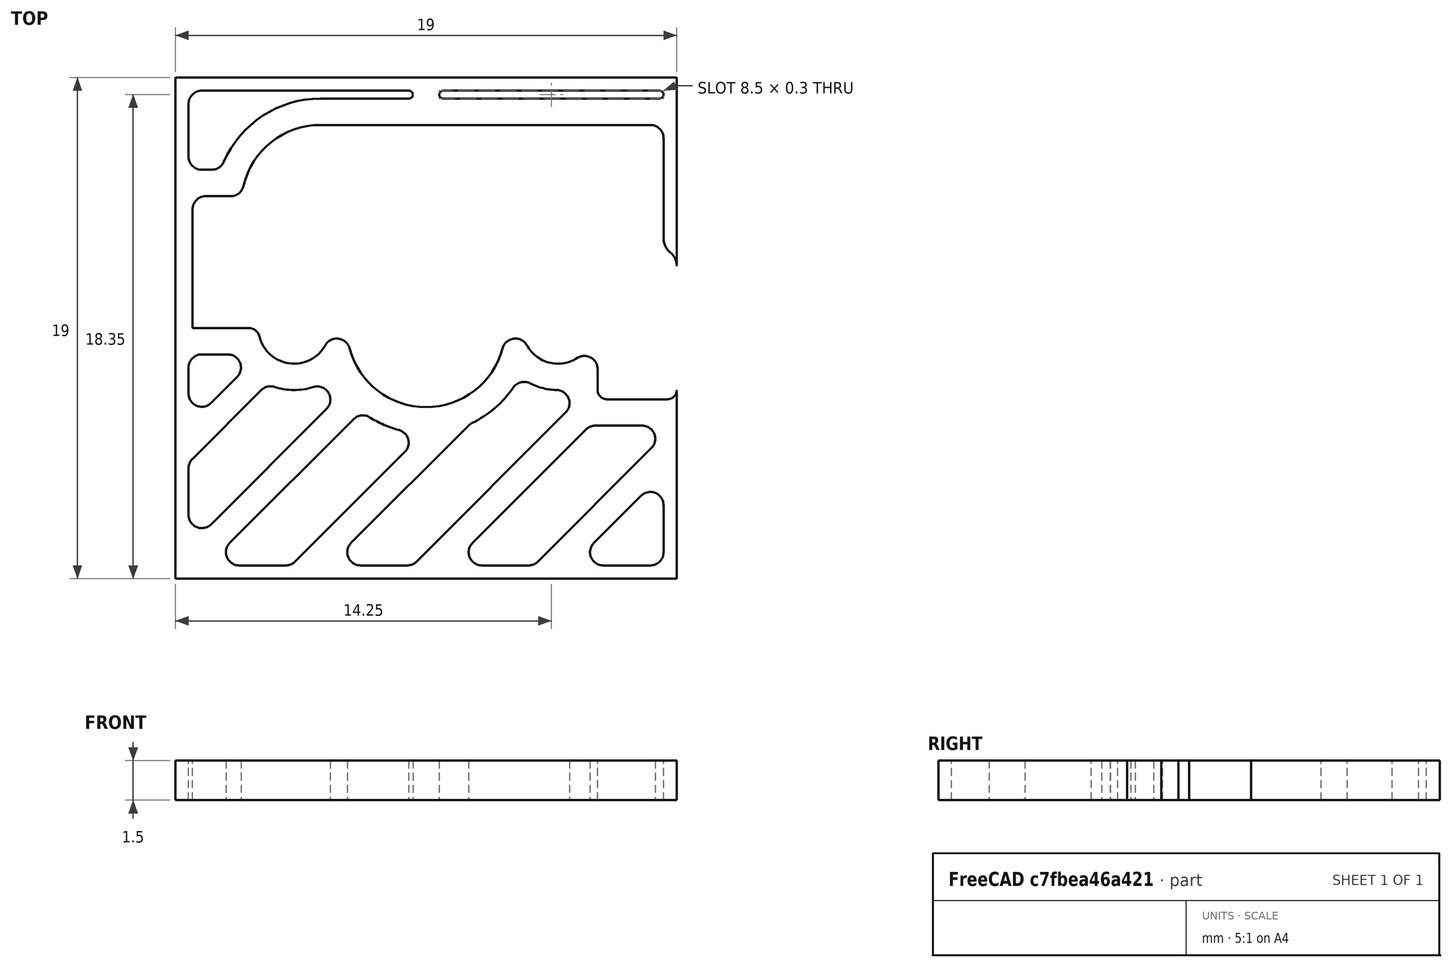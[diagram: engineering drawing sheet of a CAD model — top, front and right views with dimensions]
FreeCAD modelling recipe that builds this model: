
FCSTD DOCUMENT  (FreeCAD 0.22R36807 (Git))
Label: key-v2
License: All rights reserved
LicenseURL: https://en.wikipedia.org/wiki/All_rights_reserved
objects: Part::Part2DObjectPython×3, Sketcher::SketchObject×1, PartDesign::Pad×1, PartDesign::Body×1, Spreadsheet::Sheet×1
note: 7 computed .brp shape members not serialized (recipe doc carries the construction recipe); baked Part::Feature solids carry a one-line shape summary decoded from their .brp

FEATURE [Sketcher::SketchObject] Sketch  label="base"
  FullyConstrained = false
  sketch-geometry (148):
    g0: LineSegment StartX=-9.5 StartY=-9.5 StartZ=0 EndX=9.5 EndY=-9.5 EndZ=0
    g1: LineSegment StartX=9.5 StartY=-9.5 StartZ=0 EndX=9.5 EndY=9.5 EndZ=0
    g2: LineSegment StartX=9.5 StartY=9.5 StartZ=0 EndX=-9.5 EndY=9.5 EndZ=0
    g3: LineSegment StartX=-9.5 StartY=9.5 StartZ=0 EndX=-9.5 EndY=-9.5 EndZ=0
    g4: GeomPoint X=-1.9e-14 Y=1.95e-14 Z=0
    g5: Circle CenterX=-3.81 CenterY=2.54 CenterZ=0 NormalX=0 NormalY=0 NormalZ=1 AngleXU=0 Radius=1.5
    g6: Circle CenterX=2.54 CenterY=5.08 CenterZ=0 NormalX=0 NormalY=0 NormalZ=1 AngleXU=0 Radius=1.5
    g7: Circle CenterX=-1.9e-14 CenterY=1.95e-14 CenterZ=0 NormalX=0 NormalY=0 NormalZ=1 AngleXU=0 Radius=2
    g8: Circle CenterX=5 CenterY=-2.49e-14 CenterZ=0 NormalX=0 NormalY=0 NormalZ=1 AngleXU=0 Radius=1
    g9: Circle CenterX=-5 CenterY=-2.4746e-12 CenterZ=0 NormalX=0 NormalY=0 NormalZ=1 AngleXU=0 Radius=1
    g10: GeomPoint X=-8.5 Y=1 Z=0
    g11: GeomPoint X=-8.5 Y=4 Z=0
    g12: GeomPoint X=-6 Y=4 Z=0
    g13: GeomPoint X=-2.5 Y=1 Z=0
    g14: GeomPoint X=-0.4 Y=2.9 Z=0
    g15: GeomPoint X=4.5 Y=2.9 Z=0
    g16: GeomPoint X=4.5 Y=3.6 Z=0
    g17: GeomPoint X=7.1 Y=6.7 Z=0
    g18: GeomPoint X=-4 Y=6.7 Z=0
    g19: LineSegment StartX=-8.5 StartY=1 StartZ=0 EndX=-2.5 EndY=1 EndZ=0
    g20: LineSegment StartX=-8.5 StartY=1 StartZ=0 EndX=-8.5 EndY=4 EndZ=0
    g21: LineSegment StartX=-8.5 StartY=4 StartZ=0 EndX=-6 EndY=4 EndZ=0
    g22: LineSegment StartX=-6 StartY=4 StartZ=0 EndX=-6 EndY=4.7 EndZ=0
    g23: LineSegment StartX=-4 StartY=6.7 StartZ=0 EndX=7.1 EndY=6.7 EndZ=0
    g24: LineSegment StartX=7.1 StartY=6.7 StartZ=0 EndX=7.1 EndY=3.6 EndZ=0
    g25: LineSegment StartX=7.1 StartY=3.6 StartZ=0 EndX=4.5 EndY=3.6 EndZ=0
    g26: LineSegment StartX=4.5 StartY=2.9 StartZ=0 EndX=4.5 EndY=3.6 EndZ=0
    g27: LineSegment StartX=4.5 StartY=2.9 StartZ=0 EndX=-0.4 EndY=2.9 EndZ=0
    g28: ArcOfCircle CenterX=-0.400861 CenterY=0.790425 CenterZ=0 NormalX=0 NormalY=0 NormalZ=1 AngleXU=0 Radius=2.10958 StartAngle=1.57039 EndAngle=3.04208
    g29: LineSegment StartX=-8.14645 StartY=-7.43934 StartZ=0 EndX=-3.77376 EndY=-3.06666 EndZ=0
    g30: LineSegment StartX=-7.43934 StartY=-8.14645 StartZ=0 EndX=-2.74887 EndY=-3.45597 EndZ=0
    g31: ArcOfCircle CenterX=-1.9e-14 CenterY=1.95e-14 CenterZ=0 NormalX=0 NormalY=0 NormalZ=1 AngleXU=0 Radius=3 StartAngle=3.40116 EndAngle=6.02361
    g32: ArcOfCircle CenterX=-1.9e-14 CenterY=1.95e-14 CenterZ=0 NormalX=0 NormalY=0 NormalZ=1 AngleXU=0 Radius=4 StartAngle=4.15108 EndAngle=4.45128
    g33: LineSegment StartX=-1.9e-14 StartY=1.95e-14 StartZ=0 EndX=-9.5 EndY=-9.5 EndZ=0
    g34: LineSegment StartX=-7.51422 StartY=-1 StartZ=0 EndX=-8.5 EndY=-1 EndZ=0
    g35: ArcOfCircle CenterX=-2.39531 CenterY=-3.80953 CenterZ=0 NormalX=0 NormalY=0 NormalZ=1 AngleXU=0 Radius=0.5 StartAngle=1.00949 EndAngle=2.35619
    g36: ArcOfCircle CenterX=-1.16168 CenterY=-4.34747 CenterZ=0 NormalX=0 NormalY=0 NormalZ=1 AngleXU=0 Radius=0.5 StartAngle=5.49779 EndAngle=7.59287
    g37: ArcOfCircle CenterX=-7.08579 CenterY=-8.5 CenterZ=0 NormalX=0 NormalY=0 NormalZ=1 AngleXU=0 Radius=0.5 StartAngle=2.35619 EndAngle=4.71239
    g38: GeomPoint X=-8.29289 Y=-9 Z=0
    g39: LineSegment StartX=-9 StartY=-1.5 StartZ=0 EndX=-9 EndY=-2.48578 EndZ=0
    g40: ArcOfCircle CenterX=-8.5 CenterY=-1.5 CenterZ=0 NormalX=0 NormalY=0 NormalZ=1 AngleXU=0 Radius=0.5 StartAngle=1.5708 EndAngle=3.14159
    g41: GeomPoint X=-9 Y=-1 Z=0
    g42: ArcOfCircle CenterX=-8.5 CenterY=-7.08579 CenterZ=0 NormalX=0 NormalY=0 NormalZ=1 AngleXU=0 Radius=0.5 StartAngle=3.14159 EndAngle=5.49779
    g43: GeomPoint X=-9 Y=-8.29289 Z=0
    g44: ArcOfCircle CenterX=-5 CenterY=-2.4746e-12 CenterZ=0 NormalX=0 NormalY=0 NormalZ=1 AngleXU=0 Radius=1.35 StartAngle=3.38311 EndAngle=5.77615
    g45: ArcOfCircle CenterX=-3.38275 CenterY=-0.898333 CenterZ=0 NormalX=0 NormalY=0 NormalZ=1 AngleXU=0 Radius=0.5 StartAngle=0.259572 EndAngle=2.63456
    g46: ArcOfCircle CenterX=-1.9e-14 CenterY=1.95e-14 CenterZ=0 NormalX=0 NormalY=0 NormalZ=1 AngleXU=0 Radius=4 StartAngle=5.16472 EndAngle=5.68269
    g47: ArcOfCircle CenterX=1.96677 CenterY=-4.04745 CenterZ=0 NormalX=0 NormalY=0 NormalZ=1 AngleXU=0 Radius=0.5 StartAngle=2.02312 EndAngle=2.35619
    g48: ArcOfCircle CenterX=8.5 CenterY=-8.5 CenterZ=0 NormalX=0 NormalY=0 NormalZ=1 AngleXU=0 Radius=0.5 StartAngle=4.71239 EndAngle=6.28319
    g49: ArcOfCircle CenterX=3.71275 CenterY=-2.54273 CenterZ=0 NormalX=0 NormalY=0 NormalZ=1 AngleXU=0 Radius=0.5 StartAngle=1.10216 EndAngle=2.5411
    g50: LineSegment StartX=6.85 StartY=2.35 StartZ=0 EndX=6.85 EndY=-2.35 EndZ=0
    g51: LineSegment StartX=6.85 StartY=-2.35 StartZ=0 EndX=9.15 EndY=-2.35 EndZ=0
    g52: LineSegment StartX=9.15 StartY=-2.35 StartZ=0 EndX=9.15 EndY=2.35 EndZ=0
    g53: LineSegment StartX=9.15 StartY=2.35 StartZ=0 EndX=6.85 EndY=2.35 EndZ=0
    g54: LineSegment StartX=8.18579 StartY=-3.7 StartZ=0 EndX=6.41421 EndY=-3.7 EndZ=0
    g55: ArcOfCircle CenterX=5 CenterY=-2.49e-14 CenterZ=0 NormalX=0 NormalY=0 NormalZ=1 AngleXU=0 Radius=1.35 StartAngle=3.64863 EndAngle=5.28347
    g56: ArcOfCircle CenterX=3.38275 CenterY=-0.898333 CenterZ=0 NormalX=0 NormalY=0 NormalZ=1 AngleXU=0 Radius=0.5 StartAngle=0.507033 EndAngle=2.88202
    g57: ArcOfCircle CenterX=4.93649 CenterY=-2.84929 CenterZ=0 NormalX=0 NormalY=0 NormalZ=1 AngleXU=0 Radius=0.5 StartAngle=5.49779 EndAngle=7.8317
    g58: ArcOfCircle CenterX=6.85 CenterY=-2.35 CenterZ=0 NormalX=0 NormalY=0 NormalZ=1 AngleXU=0 Radius=0.35 StartAngle=3.14159 EndAngle=4.71239
    g59: LineSegment StartX=6.5 StartY=-2.35 StartZ=0 EndX=6.5 EndY=-1.55644 EndZ=0
    g60: ArcOfCircle CenterX=6 CenterY=-1.55644 CenterZ=0 NormalX=0 NormalY=0 NormalZ=1 AngleXU=0 Radius=0.5 StartAngle=2e-16 EndAngle=2.14188
    g61: LineSegment StartX=9.5 StartY=-2.35 StartZ=0 EndX=9.5 EndY=-9.5 EndZ=0
    g62: LineSegment StartX=9 StartY=3.39614 StartZ=0 EndX=9 EndY=7.2 EndZ=0
    g63: LineSegment StartX=8.5 StartY=7.7 StartZ=0 EndX=-4 EndY=7.7 EndZ=0
    g64: LineSegment StartX=-8.85 StartY=1.9e-15 StartZ=0 EndX=-8.85 EndY=4.5 EndZ=0
    g65: LineSegment StartX=-8.35 StartY=5 StartZ=0 EndX=-7.40735 EndY=5 EndZ=0
    g66: ArcOfCircle CenterX=9.15 CenterY=-2.35 CenterZ=0 NormalX=0 NormalY=0 NormalZ=1 AngleXU=0 Radius=0.35 StartAngle=4.71239 EndAngle=6.28319
    g67: LineSegment StartX=6.85 StartY=-2.7 StartZ=0 EndX=9.15 EndY=-2.7 EndZ=0
    g68: GeomPoint X=-8.85 Y=-0.7 Z=0
    g69: ArcOfCircle CenterX=-8.35 CenterY=4.5 CenterZ=0 NormalX=0 NormalY=0 NormalZ=1 AngleXU=0 Radius=0.5 StartAngle=1.5708 EndAngle=3.14159
    g70: GeomPoint X=-8.85 Y=5 Z=0
    g71: ArcOfCircle CenterX=-7.40735 CenterY=5.5 CenterZ=0 NormalX=0 NormalY=0 NormalZ=1 AngleXU=0 Radius=0.5 StartAngle=4.71239 EndAngle=6.05258
    g72: ArcOfCircle CenterX=8.5 CenterY=7.2 CenterZ=0 NormalX=0 NormalY=0 NormalZ=1 AngleXU=0 Radius=0.5 StartAngle=-9e-16 EndAngle=1.5708
    g73: GeomPoint X=9 Y=7.7 Z=0
    g74: LineSegment StartX=-9 StartY=8.5 StartZ=0 EndX=-9 EndY=6.5 EndZ=0
    g75: LineSegment StartX=-8.5 StartY=6 StartZ=0 EndX=-8.12432 EndY=6 EndZ=0
    g76: LineSegment StartX=-8.5 StartY=9 StartZ=0 EndX=-0.65 EndY=9 EndZ=0
    g77: ArcOfCircle CenterX=-8.12432 CenterY=6.5 CenterZ=0 NormalX=0 NormalY=0 NormalZ=1 AngleXU=0 Radius=0.5 StartAngle=4.71239 EndAngle=5.87167
    g78: ArcOfCircle CenterX=-8.5 CenterY=6.5 CenterZ=0 NormalX=0 NormalY=0 NormalZ=1 AngleXU=0 Radius=0.5 StartAngle=3.14159 EndAngle=4.71239
    g79: GeomPoint X=-9 Y=6 Z=0
    g80: ArcOfCircle CenterX=-8.5 CenterY=8.5 CenterZ=0 NormalX=0 NormalY=0 NormalZ=1 AngleXU=0 Radius=0.5 StartAngle=1.5708 EndAngle=3.14159
    g81: GeomPoint X=-9 Y=9 Z=0
    g82: ArcOfCircle CenterX=-4.12732 CenterY=-2.7131 CenterZ=0 NormalX=0 NormalY=0 NormalZ=1 AngleXU=0 Radius=0.5 StartAngle=5.49779 EndAngle=8.16519
    g83: ArcOfCircle CenterX=5 CenterY=-2.49e-14 CenterZ=0 NormalX=0 NormalY=0 NormalZ=1 AngleXU=0 Radius=2.35 StartAngle=4.24376 EndAngle=4.6901
    g84: LineSegment StartX=-4 StartY=8.7 StartZ=0 EndX=-0.65 EndY=8.7 EndZ=0
    g85: ArcOfCircle CenterX=8.85 CenterY=8.85 CenterZ=0 NormalX=0 NormalY=0 NormalZ=1 AngleXU=0 Radius=0.15 StartAngle=4.71239 EndAngle=7.85398
    g86: LineSegment StartX=6.85 StartY=-2.35 StartZ=0 EndX=-0.3 EndY=-9.5 EndZ=0
    g87: LineSegment StartX=6.06066 StartY=-3.84645 StartZ=0 EndX=1.76066 EndY=-8.14645 EndZ=0
    g88: LineSegment StartX=5.29005 StartY=-3.20285 StartZ=0 EndX=-0.36066 EndY=-8.85355 EndZ=0
    g89: LineSegment StartX=-2.83934 StartY=-8.14645 StartZ=0 EndX=1.61321 EndY=-3.69389 EndZ=0
    g90: LineSegment StartX=-4.96066 StartY=-8.85355 StartZ=0 EndX=-0.80813 EndY=-4.70102 EndZ=0
    g91: LineSegment StartX=-0.714214 StartY=-9 StartZ=0 EndX=-2.48579 EndY=-9 EndZ=0
    g92: LineSegment StartX=-5.31421 StartY=-9 StartZ=0 EndX=-7.08579 EndY=-9 EndZ=0
    g93: LineSegment StartX=-4.9 StartY=-9.5 StartZ=0 EndX=4.6 EndY=1.95e-14 EndZ=0
    g94: LineSegment StartX=-2.45 StartY=-2.45 StartZ=0 EndX=2.15 EndY=-7.05 EndZ=0
    g95: LineSegment StartX=4.3 StartY=-9.5 StartZ=0 EndX=9.5 EndY=-4.3 EndZ=0
    g96: LineSegment StartX=0.975 StartY=-3.625 StartZ=0 EndX=5.575 EndY=-8.225 EndZ=0
    g97: LineSegment StartX=4.23934 StartY=-8.85355 StartZ=0 EndX=8.53934 EndY=-4.55355 EndZ=0
    g98: LineSegment StartX=6.36066 StartY=-8.14645 StartZ=0 EndX=8.14645 EndY=-6.36066 EndZ=0
    g99: LineSegment StartX=9 StartY=-6.71421 StartZ=0 EndX=9 EndY=-8.5 EndZ=0
    g100: LineSegment StartX=6.71421 StartY=-9 StartZ=0 EndX=8.5 EndY=-9 EndZ=0
    g101: LineSegment StartX=3.88579 StartY=-9 StartZ=0 EndX=2.11421 EndY=-9 EndZ=0
    g102: ArcOfCircle CenterX=8.18579 CenterY=-4.2 CenterZ=0 NormalX=0 NormalY=0 NormalZ=1 AngleXU=0 Radius=0.5 StartAngle=5.49779 EndAngle=7.85398
    g103: ArcOfCircle CenterX=6.41421 CenterY=-4.2 CenterZ=0 NormalX=0 NormalY=0 NormalZ=1 AngleXU=0 Radius=0.5 StartAngle=1.5708 EndAngle=2.35619
    g104: GeomPoint X=6.20711 Y=-3.7 Z=0
    g105: ArcOfCircle CenterX=8.5 CenterY=-6.71421 CenterZ=0 NormalX=0 NormalY=0 NormalZ=1 AngleXU=0 Radius=0.5 StartAngle=-9e-16 EndAngle=2.35619
    g106: GeomPoint X=9 Y=-5.50711 Z=0
    g107: ArcOfCircle CenterX=6.71421 CenterY=-8.5 CenterZ=0 NormalX=0 NormalY=0 NormalZ=1 AngleXU=0 Radius=0.5 StartAngle=2.35619 EndAngle=4.71239
    g108: GeomPoint X=5.50711 Y=-9 Z=0
    g109: ArcOfCircle CenterX=3.88579 CenterY=-8.5 CenterZ=0 NormalX=0 NormalY=0 NormalZ=1 AngleXU=0 Radius=0.5 StartAngle=4.71239 EndAngle=5.49779
    g110: GeomPoint X=4.09289 Y=-9 Z=0
    g111: ArcOfCircle CenterX=2.11421 CenterY=-8.5 CenterZ=0 NormalX=0 NormalY=0 NormalZ=1 AngleXU=0 Radius=0.5 StartAngle=2.35619 EndAngle=4.71239
    g112: GeomPoint X=0.907107 Y=-9 Z=0
    g113: ArcOfCircle CenterX=-2.48579 CenterY=-8.5 CenterZ=0 NormalX=0 NormalY=0 NormalZ=1 AngleXU=0 Radius=0.5 StartAngle=2.35619 EndAngle=4.71239
    g114: GeomPoint X=-3.69289 Y=-9 Z=0
    g115: ArcOfCircle CenterX=-0.714214 CenterY=-8.5 CenterZ=0 NormalX=0 NormalY=0 NormalZ=1 AngleXU=0 Radius=0.5 StartAngle=4.71239 EndAngle=5.49779
    g116: GeomPoint X=-0.507107 Y=-9 Z=0
    g117: ArcOfCircle CenterX=-5.31421 CenterY=-8.5 CenterZ=0 NormalX=0 NormalY=0 NormalZ=1 AngleXU=0 Radius=0.5 StartAngle=4.71239 EndAngle=5.49779
    g118: GeomPoint X=-5.10711 Y=-9 Z=0
    g119: LineSegment StartX=-9.5 StartY=-9.5 StartZ=0 EndX=9.5 EndY=-9.5 EndZ=0
    g120: ArcOfCircle CenterX=9.67221 CenterY=3.39614 CenterZ=0 NormalX=0 NormalY=0 NormalZ=1 AngleXU=0 Radius=0.672207 StartAngle=3.14159 EndAngle=4.03329
    g121: ArcOfCircle CenterX=8.82779 CenterY=2.35 CenterZ=0 NormalX=0 NormalY=0 NormalZ=1 AngleXU=0 Radius=0.672207 StartAngle=0 EndAngle=0.891699
    g122: LineSegment StartX=9.5 StartY=2.35 StartZ=0 EndX=9.09006 EndY=3.06004 EndZ=0
    g123: LineSegment StartX=9.5 StartY=2.35 StartZ=0 EndX=9.5 EndY=9.5 EndZ=0
    g124: LineSegment StartX=9.5 StartY=9.5 StartZ=0 EndX=-9.5 EndY=9.5 EndZ=0
    g125: ArcOfCircle CenterX=-4 CenterY=4.7 CenterZ=0 NormalX=0 NormalY=0 NormalZ=1 AngleXU=0 Radius=4 StartAngle=1.5708 EndAngle=2.73008
    g126: ArcOfCircle CenterX=-4 CenterY=4.7 CenterZ=0 NormalX=0 NormalY=0 NormalZ=1 AngleXU=0 Radius=3 StartAngle=1.5708 EndAngle=2.91098
    g127: ArcOfCircle CenterX=-4 CenterY=4.7 CenterZ=0 NormalX=0 NormalY=0 NormalZ=1 AngleXU=0 Radius=2 StartAngle=1.5708 EndAngle=3.14159
    g128: ArcOfCircle CenterX=-0.65 CenterY=8.85 CenterZ=0 NormalX=0 NormalY=0 NormalZ=1 AngleXU=0 Radius=0.15 StartAngle=4.71239 EndAngle=7.85398
    g129: LineSegment StartX=0.65 StartY=9 StartZ=0 EndX=8.85 EndY=9 EndZ=0
    g130: LineSegment StartX=0.65 StartY=8.7 StartZ=0 EndX=8.85 EndY=8.7 EndZ=0
    g131: ArcOfCircle CenterX=0.65 CenterY=8.85 CenterZ=0 NormalX=0 NormalY=0 NormalZ=1 AngleXU=0 Radius=0.15 StartAngle=1.5708 EndAngle=4.71239
    g132: LineSegment StartX=-9.5 StartY=-4.89999 StartZ=0 EndX=-4.60001 EndY=1.95e-14 EndZ=0
    g133: LineSegment StartX=-7.05 StartY=-2.45 StartZ=0 EndX=-2.45 EndY=-7.05 EndZ=0
    g134: LineSegment StartX=-8.85355 StartY=-4.96065 StartZ=0 EndX=-6.24601 EndY=-2.35311 EndZ=0
    g135: ArcOfCircle CenterX=-5 CenterY=-2.4746e-12 CenterZ=0 NormalX=0 NormalY=0 NormalZ=1 AngleXU=0 Radius=2.35 StartAngle=4.39389 EndAngle=5.02359
    g136: LineSegment StartX=-9 StartY=-5.31421 StartZ=0 EndX=-9 EndY=-7.08579 EndZ=0
    g137: LineSegment StartX=-8.14645 StartY=-2.83933 StartZ=0 EndX=-7.16067 EndY=-1.85355 EndZ=0
    g138: ArcOfCircle CenterX=-5.89246 CenterY=-2.70666 CenterZ=0 NormalX=0 NormalY=0 NormalZ=1 AngleXU=0 Radius=0.5 StartAngle=1.2523 EndAngle=2.35619
    g139: ArcOfCircle CenterX=-8.5 CenterY=-5.31421 CenterZ=0 NormalX=0 NormalY=0 NormalZ=1 AngleXU=0 Radius=0.5 StartAngle=2.35619 EndAngle=3.14159
    g140: GeomPoint X=-9 Y=-5.1071 Z=0
    g141: ArcOfCircle CenterX=-8.5 CenterY=-2.48578 CenterZ=0 NormalX=0 NormalY=0 NormalZ=1 AngleXU=0 Radius=0.5 StartAngle=3.14159 EndAngle=5.49779
    g142: GeomPoint X=-9 Y=-3.69289 Z=0
    g143: ArcOfCircle CenterX=-7.51422 CenterY=-1.5 CenterZ=0 NormalX=0 NormalY=0 NormalZ=1 AngleXU=0 Radius=0.5 StartAngle=5.49779 EndAngle=7.85398
    g144: GeomPoint X=-6.30711 Y=-1 Z=0
    g145: LineSegment StartX=-9.5 StartY=9.5 StartZ=0 EndX=-9.5 EndY=-9.5 EndZ=0
    g146: LineSegment StartX=-8.85 StartY=1.9e-15 StartZ=0 EndX=-6.72288 EndY=1.9e-15 EndZ=0
    g147: ArcOfCircle CenterX=-6.72288 CenterY=-0.424382 CenterZ=0 NormalX=0 NormalY=0 NormalZ=1 AngleXU=0 Radius=0.424382 StartAngle=0.241513 EndAngle=1.5708
  constraints (336):
    c: Coincident(g0,g1)
    c: Coincident(g1,g2)
    c: Coincident(g2,g3)
    c: Horizontal(g0)
    c: Horizontal(g2)
    c: Vertical(g1)
    c: Symmetric(g2,g0,g4)
    c: Coincident(g4,g-1)
    c: Coincident(g7,g4)
    c: PointOnObject(g8,g-1)
    c: Equal(g5,g6)
    c: Symmetric(g8,g9,g-2)
    c: Equal(g9,g8)
    c: DistanceX(g-1,g6) = 2.54
    c: Distance(g6,g-1) = 5.08
    c: DistanceX(g2,g2) = 19
    c: Equal(g2,g3)
    c: Distance(g5,g-2) = 3.81
    c: Distance(g5,g-1) = 2.54
    c: Distance(g9,g-2) = 5
    c: Distance(g10,g-1) = 1
    c: Coincident(g19,g10)
    c: Coincident(g19,g13)
    c: Horizontal(g19)
    c: Distance(g10,g-2) = 8.5
    c: Coincident(g20,g10)
    c: Coincident(g20,g11)
    c: Vertical(g20)
    c: Distance(g11,g-1) = 4
    c: Coincident(g21,g11)
    c: Coincident(g21,g12)
    c: Horizontal(g21)
    c: Distance(g12,g-2) = 6
    c: Distance(g18,g-2) = 4
    c: DistanceY(g-1,g18) = 6.7
    c: Coincident(g22,g12)
    c: Vertical(g22)
    c: Coincident(g23,g18)
    c: Coincident(g23,g17)
    c: Horizontal(g23)
    c: DistanceX(g-1,g17) = 7.1
    c: Coincident(g24,g17)
    c: Vertical(g24)
    c: Distance(g24,g-1) = 3.6
    c: Coincident(g25,g24)
    c: Coincident(g25,g16)
    c: Coincident(g26,g15)
    c: Coincident(g26,g16)
    c: Coincident(g27,g15)
    c: Coincident(g27,g14)
    c: Horizontal(g25)
    c: Horizontal(g27)
    c: Vertical(g26)
    c: Distance(g-2,g26) = 4.5
    c: Distance(g15,g-1) = 2.9
    c: Distance(g14,g-2) = 0.4
    c: Distance(g13,g-2) = 2.5
    c: Coincident(g28,g14)
    c: Coincident(g28,g13)
    c: Diameter(g6) = 3
    c: Diameter(g9) = 2
    c: Diameter(g7) = 4
    c: Parallel(g30,g29)
    c: Distance(g31,g7) = 1
    c: Coincident(g32,g31)
    c: Symmetric(g38,g43,g33)
    c: Horizontal(g34)
    c: Distance(g43,g30) = 1
    c: Tangent(g30,g35) = 1.5708
    c: Tangent(g32,g35) = 1.5708
    c: Tangent(g32,g36) = 1.5708
    c: PointOnObject(g38,g30)
    c: Tangent(g30,g37) = 1.5708
    c: Vertical(g39)
    c: PointOnObject(g41,g34)
    c: PointOnObject(g41,g39)
    c: Tangent(g34,g40) = -1.5708
    c: Tangent(g39,g40) = -1.5708
    c: PointOnObject(g43,g39)
    c: PointOnObject(g43,g29)
    c: Tangent(g29,g42) = -1.5708
    c: Equal(g42,g35)
    c: Equal(g35,g36)
    c: Coincident(g44,g9)
    c: Radius(g40) = 0.5
    c: Distance(g32,g31) = 1
    c: Tangent(g45,g31) = 1.5708
    c: Tangent(g45,g44) = 1.5708
    c: Coincident(g46,g31)
    c: Equal(g46,g32)
    c: Equal(g49,g36)
    c: Coincident(g50,g51)
    c: Coincident(g51,g52)
    c: Coincident(g52,g53)
    c: Coincident(g53,g50)
    c: Vertical(g52)
    c: Horizontal(g51)
    c: Horizontal(g53)
    c: Distance(g50,g-2) = 6.85
    c: Distance(g50,g-1) = 2.35
    c: Symmetric(g50,g50,g-1)
    c: DistanceX(g53,g53) = 2.3
    c: Horizontal(g54)
    c: Coincident(g55,g8)
    c: Distance(g55,g8) = 0.35
    c: Tangent(g56,g31) = 1.5708
    c: Tangent(g56,g55) = 1.5708
    c: Radius(g58) = 0.35
    c: PointOnObject(g61,g1)
    c: Vertical(g59)
    c: Tangent(g60,g55) = 1.5708
    c: Tangent(g60,g59) = -1.5708
    c: Equal(g60,g57)
    c: Equal(g56,g57)
    c: Tangent(g56,g31,g31) = 1.5708
    c: Tangent(g59,g58) = 1.5708
    c: Vertical(g61)
    c: Distance(g44,g9) = 0.35
    c: Distance(g146,g34) = 1
    c: Horizontal(g63)
    c: Vertical(g64)
    c: Horizontal(g65)
    c: Vertical(g62)
    c: Horizontal(g67)
    c: Equal(g66,g58)
    c: Tangent(g67,g66) = -1.5708
    c: Tangent(g66,g61) = 1.5708
    c: Tangent(g67,g58) = -1.5708
    c: Distance(g68,g20) = 0.35
    c: PointOnObject(g68,g64)
    c: Distance(g73,g23) = 1
    c: Distance(g21,g65) = 1
    c: PointOnObject(g70,g65)
    c: PointOnObject(g70,g64)
    c: Tangent(g65,g69) = 1.5708
    c: Tangent(g64,g69) = 1.5708
    c: Tangent(g65,g71) = -1.5708
    c: Equal(g71,g69)
    c: PointOnObject(g73,g63)
    c: PointOnObject(g73,g62)
    c: Tangent(g63,g72) = -1.5708
    c: Tangent(g62,g72) = -1.5708
    c: Equal(g72,g71)
    c: Vertical(g74)
    c: Horizontal(g75)
    c: Horizontal(g76)
    c: Tangent(g75,g77) = -1.5708
    c: PointOnObject(g79,g74)
    c: PointOnObject(g79,g75)
    c: Tangent(g74,g78) = -1.5708
    c: Tangent(g75,g78) = -1.5708
    c: PointOnObject(g81,g74)
    c: PointOnObject(g81,g76)
    c: Tangent(g74,g80) = -1.5708
    c: Tangent(g76,g80) = 1.5708
    c: Distance(g65,g75) = 1
    c: Parallel(g30,g33)
    c: Tangent(g82,g29) = -1.5708
    c: Equal(g82,g40)
    c: Equal(g45,g82)
    c: Equal(g42,g40)
    c: Coincident(g83,g55)
    c: Distance(g83,g55) = 1
    c: Tangent(g49,g83) = 1.5708
    c: Tangent(g57,g83) = 1.5708
    c: Equal(g56,g49)
    c: Distance(g54,g67) = 1
    c: Equal(g47,g36)
    c: Tangent(g47,g46) = 1.5708
    c: Distance(g85,g1) = 0.5
    c: Equal(g80,g77)
    c: Equal(g78,g69)
    c: PointOnObject(g86,g0)
    c: Angle(g0,g86) = 0.785398
    c: Parallel(g88,g86)
    c: Parallel(g86,g87)
    c: Distance(g104,g86) = 0.5
    c: Distance(g86,g88) = 0.5
    c: Tangent(g57,g88) = 1.5708
    c: Parallel(g90,g89)
    c: Horizontal(g91)
    c: Tangent(g92,g91)
    c: Distance(g0,g91) = 0.5
    c: Tangent(g36,g90) = -1.5708
    c: Tangent(g47,g89) = 1.5708
    c: PointOnObject(g93,g0)
    c: Parallel(g93,g33)
    c: PointOnObject(g94,g33)
    c: PointOnObject(g94,g86)
    c: Distance(g118,g93) = 0.5
    c: Parallel(g89,g93)
    c: Distance(g93,g89) = 0.5
    c: Tangent(g46,g49) = 1.5708
    c: PointOnObject(g95,g0)
    c: PointOnObject(g95,g1)
    c: Parallel(g95,g33)
    c: PointOnObject(g96,g93)
    c: PointOnObject(g96,g95)
    c: Vertical(g99)
    c: Parallel(g97,g98)
    c: Parallel(g98,g95)
    c: Distance(g95,g97) = 0.5
    c: Distance(g108,g95) = 0.5
    c: Distance(g61,g99) = 0.5
    c: Tangent(g102,g54) = -1.5708
    c: Tangent(g102,g97) = -1.5708
    c: Tangent(g48,g99) = 1.5708
    c: Tangent(g100,g48) = -1.5708
    c: Horizontal(g93,g4)
    c: PointOnObject(g104,g54)
    c: PointOnObject(g104,g87)
    c: Tangent(g54,g103) = -1.5708
    c: Tangent(g87,g103) = -1.5708
    c: PointOnObject(g106,g98)
    c: PointOnObject(g106,g99)
    c: Tangent(g98,g105) = 1.5708
    c: Tangent(g99,g105) = 1.5708
    c: PointOnObject(g108,g98)
    c: PointOnObject(g108,g100)
    c: Tangent(g98,g107) = 1.5708
    c: Tangent(g100,g107) = -1.5708
    c: PointOnObject(g110,g97)
    c: PointOnObject(g110,g101)
    c: Tangent(g97,g109) = -1.5708
    c: Tangent(g101,g109) = 1.5708
    c: PointOnObject(g112,g87)
    c: PointOnObject(g112,g101)
    c: Tangent(g87,g111) = -1.5708
    c: Tangent(g101,g111) = 1.5708
    c: PointOnObject(g114,g91)
    c: PointOnObject(g114,g89)
    c: Tangent(g91,g113) = 1.5708
    c: Tangent(g89,g113) = 1.5708
    c: PointOnObject(g116,g91)
    c: PointOnObject(g116,g88)
    c: Tangent(g91,g115) = 1.5708
    c: Tangent(g88,g115) = 1.5708
    c: Equal(g102,g103)
    c: Equal(g103,g111)
    c: Equal(g111,g109)
    c: Equal(g109,g57)
    c: Equal(g105,g107)
    c: Equal(g107,g48)
    c: Equal(g48,g57)
    c: Tangent(g92,g101)
    c: Tangent(g100,g92)
    c: Equal(g115,g113)
    c: Equal(g113,g57)
    c: PointOnObject(g118,g92)
    c: PointOnObject(g118,g90)
    c: Tangent(g92,g117) = 1.5708
    c: Tangent(g90,g117) = -1.5708
    c: Equal(g117,g37)
    c: Equal(g37,g35)
    c: Distance(g3,g39) = 0.5
    c: Coincident(g119,g3)
    c: Coincident(g119,g61)
    c: Horizontal(g119)
    c: Coincident(g3,g0)
    c: Vertical(g3)
    c: Tangent(g92,g37) = 1.5708
    c: Equal(g78,g80)
    c: Distance(g3,g74) = 0.5
    c: Distance(g2,g76) = 0.5
    c: Tangent(g120,g62) = 1.5708
    c: Distance(g1,g62) = 0.5
    c: Tangent(g121,g1) = -1.5708
    c: Tangent(g121,g120) = 1.5708
    c: Equal(g121,g120)
    c: Horizontal(g121,g52)
    c: Coincident(g122,g121)
    c: Tangent(g122,g120) = 1.5708
    c: Angle(g1,g122) = 0.523599
    c: Coincident(g123,g121)
    c: Coincident(g123,g1)
    c: Coincident(g124,g1)
    c: Coincident(g124,g2)
    c: Tangent(g125,g84) = 1.5708
    c: Tangent(g125,g77) = 1.5708
    c: Vertical(g63,g18)
    c: Tangent(g126,g63) = -1.5708
    c: Tangent(g126,g71) = 1.5708
    c: Distance(g63,g84) = 1
    c: Coincident(g127,g18)
    c: Tangent(g127,g22) = 1.5708
    c: Coincident(g125,g126)
    c: Coincident(g125,g127)
    c: Tangent(g76,g128) = 1.5708
    c: Tangent(g84,g128) = -1.5708
    c: Tangent(g129,g76)
    c: Tangent(g130,g84)
    c: Tangent(g85,g130) = -1.5708
    c: Tangent(g85,g129) = 1.5708
    c: Tangent(g131,g129) = 1.5708
    c: Tangent(g131,g130) = -1.5708
    c: Symmetric(g128,g131,g-2)
    c: Distance(g128,g131) = 1
    c: PointOnObject(g132,g3)
    c: Parallel(g132,g33)
    c: PointOnObject(g133,g132)
    c: PointOnObject(g133,g93)
    c: Horizontal(g132,g4)
    c: Parallel(g134,g132)
    c: Distance(g140,g132) = 0.5
    c: Parallel(g137,g132)
    c: Distance(g132,g137) = 0.5
    c: Tangent(g134,g138) = 1.5708
    c: Tangent(g135,g138) = 1.5708
    c: PointOnObject(g140,g136)
    c: PointOnObject(g140,g134)
    c: Tangent(g136,g139) = -1.5708
    c: Tangent(g134,g139) = 1.5708
    c: PointOnObject(g142,g39)
    c: PointOnObject(g142,g137)
    c: Tangent(g39,g141) = -1.5708
    c: Tangent(g137,g141) = -1.5708
    c: PointOnObject(g144,g137)
    c: PointOnObject(g144,g34)
    c: Tangent(g137,g143) = -1.5708
    c: Tangent(g34,g143) = -1.5708
    c: Equal(g143,g141)
    c: Equal(g141,g139)
    c: Equal(g139,g138)
    c: Equal(g138,g40)
    c: Distance(g135,g44) = 1
    c: Coincident(g135,g9)
    c: Tangent(g82,g135) = 1.5708
    c: Tangent(g136,g42) = -1.5708
    c: Tangent(g136,g39)
    c: Coincident(g145,g2)
    c: Coincident(g145,g0)
    c: Horizontal(g146)
    c: Distance(g19,g146) = 1
    c: Coincident(g146,g64)
    c: Tangent(g147,g146) = 1.5708
    c: Tangent(g147,g44) = 1.5708
FEATURE [PartDesign::Pad] Pad
  Direction = (0,0,1)
  Length = 1.5
  Length2 = 10
  Profile = -> Sketch
  ReferenceAxis = -> Sketch [N_Axis]
  Refine = true
  Suppressed = false
  Type = 0
FEATURE [PartDesign::Body] Body  label="underbutton"
  Group = -> [Sketch,Pad]
  Origin = -> Origin
  Tip = -> Pad
FEATURE [Spreadsheet::Sheet] Spreadsheet  label="constants"
  cells = A1(slot_height)=0.6; B1='slot height; A2(base_normal)=1.5; B2='base normal; A3(base_thin)=0.3; B3='base thin ; A4(fillet_small)=0.15; B4='fillet rounding
FEATURE [Part::Part2DObjectPython] Wire  # Draft 2D object (typed FeaturePython)
  Area = 0
  ChamferSize = 0
  Closed = false
  End = (95,2.6,0)
  FilletRadius = 0
  Length = 95.9778
  MakeFace = true
  Points = (6) [(0,0,0),(19,0,0),(38,4.8,0),(57,7,0),(76,4.8,0),(95,2.6,0)]
  Start = (0,0,0)
  Subdivisions = 0
FEATURE [Part::Part2DObjectPython] Wire001  label="main matrix wire"  # Draft 2D object (typed FeaturePython)
  Area = 0
  ChamferSize = 0
  Closed = false
  End = (95,2.6,0)
  FilletRadius = 0
  Length = 323.978
  MakeFace = false
  Points = (18) [(0,0,0),(0,-19,0),(0,-38,0),(19,-38,0),(19,-19,0),(19,0,0),(38,4.8,0),(38,-14.2,0),(38,-33.2,0),(57,-31,0),(57,-12,0),(57,7,0),(76,4.8,0),+5 more]
  Start = (0,0,0)
  Subdivisions = 0
FEATURE [Part::Part2DObjectPython] Wire002  label="full matrix"  # Draft 2D object (typed FeaturePython)
  Area = 0
  ChamferSize = 0
  Closed = false
  End = (95,2.6,0)
  FilletRadius = 0
  Length = 424.206
  MakeFace = true
  Points = (22) [(0,0,0),(0,-19,0),(0,-38,0),(19,-38,0),(19,-19,0),(19,0,0),(38,4.8,0),(38,-14.2,0),(38,-33.2,0),(47,-52.4,0),(66,-52.4,0),(57,-31,0),(57,-12,0),+9 more]
  Start = (0,0,0)
  Subdivisions = 0
